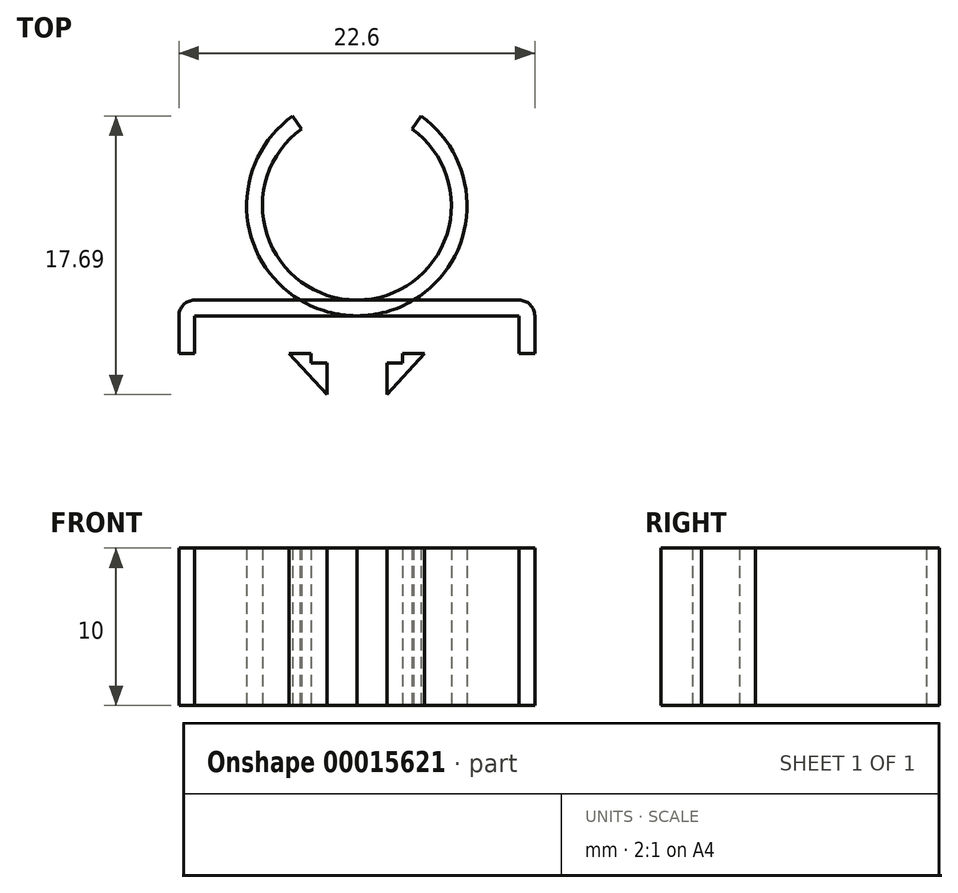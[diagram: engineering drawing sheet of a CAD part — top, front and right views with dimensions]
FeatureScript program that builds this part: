
annotation { "Feature Type Name" : "Feature", "Feature Type Description" : "" }
export const myFeature = defineFeature(function(context is Context, id is Id, definition is map)
    precondition{}
    {
        {
            var Q0;
            Q0=qCreatedBy(makeId("Top.planeOp"),FACE);
            var sketch = newSketch(context, id + "F0", { "sketchPlane" : qUnion([Q0])});
            skCircle(sketch, "E0", {"center": v(0, 0) * mm, "radius": 6 * mm});
            skCircle(sketch, "E1", {"center": v(0, 0) * mm, "radius": 7 * mm});
            skLineSegment(sketch, "E2.bottom", {"start": v(-3.5, 0) * mm, "end": v(3.5, 0) * mm});
            skLineSegment(sketch, "E2.top", {"start": v(-3.5, 10.18) * mm, "end": v(3.5, 10.18) * mm});
            skLineSegment(sketch, "E2.left", {"start": v(-3.5, 0) * mm, "end": v(-3.5, 10.18) * mm});
            skLineSegment(sketch, "E2.right", {"start": v(3.5, 0) * mm, "end": v(3.5, 10.18) * mm});
            skLineSegment(sketch, "E3.bottom", {"start": v(-10.3, -7) * mm, "end": v(10.3, -7) * mm});
            skLineSegment(sketch, "E3.top", {"start": v(-10.3, -6) * mm, "end": v(10.3, -6) * mm});
            skLineSegment(sketch, "E3.left", {"start": v(-10.3, -7) * mm, "end": v(-10.3, -6) * mm});
            skLineSegment(sketch, "E3.right", {"start": v(10.3, -7) * mm, "end": v(10.3, -6) * mm});
            skLineSegment(sketch, "E4", {"start": v(0, 0) * mm, "end": v(0, -7) * mm, "construction": true});
            skLineSegment(sketch, "E5", {"start": v(3.5, 4.87) * mm, "end": v(4.08, 5.69) * mm});
            skLineSegment(sketch, "E6", {"start": v(-3.5, 4.87) * mm, "end": v(-4.08, 5.69) * mm});
            skLineSegment(sketch, "E7.bottom", {"start": v(10.3, -7) * mm, "end": v(11.3, -7) * mm});
            skLineSegment(sketch, "E7.top", {"start": v(10.3, -9.4) * mm, "end": v(11.3, -9.4) * mm});
            skLineSegment(sketch, "E7.left", {"start": v(10.3, -7) * mm, "end": v(10.3, -9.4) * mm});
            skLineSegment(sketch, "E7.right", {"start": v(11.3, -7) * mm, "end": v(11.3, -9.4) * mm});
            skArc(sketch, "E8", {"start": v(11.3, -7) * mm, "mid": v(11, -6.3) * mm, "end": v(10.3, -6) * mm});
            skLineSegment(sketch, "E9.bottom", {"start": v(-10.3, -7) * mm, "end": v(-11.3, -7) * mm});
            skLineSegment(sketch, "E9.top", {"start": v(-10.3, -9.4) * mm, "end": v(-11.3, -9.4) * mm});
            skLineSegment(sketch, "E9.left", {"start": v(-10.3, -7) * mm, "end": v(-10.3, -9.4) * mm});
            skLineSegment(sketch, "E9.right", {"start": v(-11.3, -7) * mm, "end": v(-11.3, -9.4) * mm});
            skArc(sketch, "E10", {"start": v(-10.3, -6) * mm, "mid": v(-11, -6.3) * mm, "end": v(-11.3, -7) * mm});
            skLineSegment(sketch, "E11", {"start": v(-2.9, -7) * mm, "end": v(2.9, -7) * mm, "construction": true});
            skLineSegment(sketch, "E12.bottom", {"start": v(-2.9, -7) * mm, "end": v(-1.9, -7) * mm});
            skLineSegment(sketch, "E12.top", {"start": v(-2.9, -10) * mm, "end": v(-1.9, -10) * mm});
            skLineSegment(sketch, "E12.left", {"start": v(-2.9, -7) * mm, "end": v(-2.9, -10) * mm});
            skLineSegment(sketch, "E12.right", {"start": v(-1.9, -7) * mm, "end": v(-1.9, -10) * mm});
            skLineSegment(sketch, "E13.bottom", {"start": v(2.9, -7) * mm, "end": v(1.9, -7) * mm});
            skLineSegment(sketch, "E13.top", {"start": v(2.9, -10) * mm, "end": v(1.9, -10) * mm});
            skLineSegment(sketch, "E13.left", {"start": v(2.9, -7) * mm, "end": v(2.9, -10) * mm});
            skLineSegment(sketch, "E13.right", {"start": v(1.9, -7) * mm, "end": v(1.9, -10) * mm});
            skLineSegment(sketch, "E14", {"start": v(4.3, -9.4) * mm, "end": v(2.9, -9.4) * mm});
            skLineSegment(sketch, "E15", {"start": v(-2.9, -9.4) * mm, "end": v(-4.3, -9.4) * mm});
            skLineSegment(sketch, "E16", {"start": v(-2.9, -9.4) * mm, "end": v(2.9, -9.4) * mm, "construction": true});
            skLineSegment(sketch, "E17", {"start": v(1.9, -10) * mm, "end": v(1.9, -12) * mm});
            skLineSegment(sketch, "E18", {"start": v(1.9, -12) * mm, "end": v(4.3, -9.4) * mm});
            skLineSegment(sketch, "E19", {"start": v(-1.9, -10) * mm, "end": v(-1.9, -12) * mm});
            skLineSegment(sketch, "E20", {"start": v(-1.9, -12) * mm, "end": v(-4.3, -9.4) * mm});
            skSolve(sketch);
        }
        {
            var Q0;
            Q0=makeQuery(id+"F0.imprint","IMPRINT",FACE,{"disambiguationData":[TD([[makeQuery(id+"F0.imprint","IMPRINT",EDGE,{"derivedFrom":sQuery(id+"F0.wireOp",EDGE,"E7.bottom")}),-1.0]])]});
            var Q1;
            Q1=makeQuery(id+"F0.imprint","IMPRINT",FACE,{"disambiguationData":[TD([[makeQuery(id+"F0.imprint","IMPRINT",EDGE,{"derivedFrom":sQuery(id+"F0.wireOp",EDGE,"E9.bottom")}),1.0]])]});
            var Q2;
            {var subQ1=sQuery(id+"F0.wireOp",EDGE,"E15");Q2=makeQuery(id+"F0.imprint","IMPRINT",FACE,{"disambiguationData":[TD([[makeQuery(id+"F0.imprint","IMPRINT",EDGE,{"derivedFrom":subQ1}),1.0]])]});}
            var Q3;
            {var subQ1=sQuery(id+"F0.wireOp",EDGE,"7c9eb7b9-ca48-4d36-bab2-391d59fa54ff");Q3=makeQuery(id+"F0.imprint","IMPRINT",FACE,{"disambiguationData":[TD([[makeQuery(id+"F0.imprint","IMPRINT",EDGE,{"derivedFrom":subQ1}),-1.0]])]});}
            var Q4;
            Q4=makeQuery(id+"F0.imprint","IMPRINT",FACE,{"disambiguationData":[TD([[makeQuery(id+"F0.imprint","IMPRINT",EDGE,{"derivedFrom":sQuery(id+"F0.wireOp",EDGE,"E3.left")}),1.0]])]});
            var Q5;
            Q5=makeQuery(id+"F0.imprint","IMPRINT",FACE,{"disambiguationData":[TD([[makeQuery(id+"F0.imprint","IMPRINT",EDGE,{"derivedFrom":sQuery(id+"F0.wireOp",EDGE,"E3.right")}),-1.0]])]});
            var Q6;
            {var subQ3=sQuery(id+"F0.wireOp",EDGE,"E12.bottom");Q6=makeQuery(id+"F0.imprint","IMPRINT",FACE,{"disambiguationData":[TD([[makeQuery(id+"F0.imprint","IMPRINT",EDGE,{"derivedFrom":subQ3}),-1.0]])]});}
            var Q7;
            {var subQ2=sQuery(id+"F0.wireOp",EDGE,"E13.bottom");Q7=makeQuery(id+"F0.imprint","IMPRINT",FACE,{"disambiguationData":[TD([[makeQuery(id+"F0.imprint","IMPRINT",EDGE,{"derivedFrom":subQ2}),1.0]])]});}
            var Q8;
            {var subQ0=sQuery(id+"F0.wireOp",EDGE,"E6");Q8=makeQuery(id+"F0.imprint","IMPRINT",FACE,{"disambiguationData":[TD([[makeQuery(id+"F0.imprint","IMPRINT",EDGE,{"derivedFrom":subQ0}),1.0]])]});}
            var Q9;
            {var subQ0=sQuery(id+"F0.wireOp",EDGE,"E5");Q9=makeQuery(id+"F0.imprint","IMPRINT",FACE,{"disambiguationData":[TD([[makeQuery(id+"F0.imprint","IMPRINT",EDGE,{"derivedFrom":subQ0}),-1.0]])]});}
            var Q10;
            {var subQ1=sQuery(id+"F0.wireOp",EDGE,"E3.left");Q10=makeQuery(id+"F0.imprint","IMPRINT",FACE,{"disambiguationData":[TD([[makeQuery(id+"F0.imprint","IMPRINT",EDGE,{"derivedFrom":subQ1}),-1.0]])]});}
            var Q11;
            {var subQ1=sQuery(id+"F0.wireOp",EDGE,"E3.right");Q11=makeQuery(id+"F0.imprint","IMPRINT",FACE,{"disambiguationData":[TD([[makeQuery(id+"F0.imprint","IMPRINT",EDGE,{"derivedFrom":subQ1}),1.0]])]});}
            var Q12;
            {var subQ0=sQuery(id+"F0.wireOp",EDGE,"E3.top");var subQ2=sQuery(id+"F0.wireOp",EDGE,"E1");var subQ4=makeQuery(id+"F0.imprint","INTERSECT",VERTEX,{"disambiguationData":[OD(0.0)],"derivedFrom":[subQ2,subQ0]});Q12=makeQuery(id+"F0.imprint","IMPRINT",FACE,{"disambiguationData":[TD([[makeQuery(id+"F0.imprint","IMPRINT",EDGE,{"disambiguationData":[TD([[subQ4,-1.0]])],"derivedFrom":subQ2}),1.0]])]});}
            var Q13;
            {var subQ2=sQuery(id+"F0.wireOp",EDGE,"E13.top");Q13=makeQuery(id+"F0.imprint","IMPRINT",FACE,{"disambiguationData":[TD([[makeQuery(id+"F0.imprint","IMPRINT",EDGE,{"derivedFrom":subQ2}),1.0]])]});}
            extrude(context, id + "F1", {"entities" : qUnion([Q0, Q1, Q2, Q3, Q4, Q5, Q6, Q7, Q8, Q9, Q10, Q11, Q12, Q13]), "depth" : 10 * mm});
        }
    });
